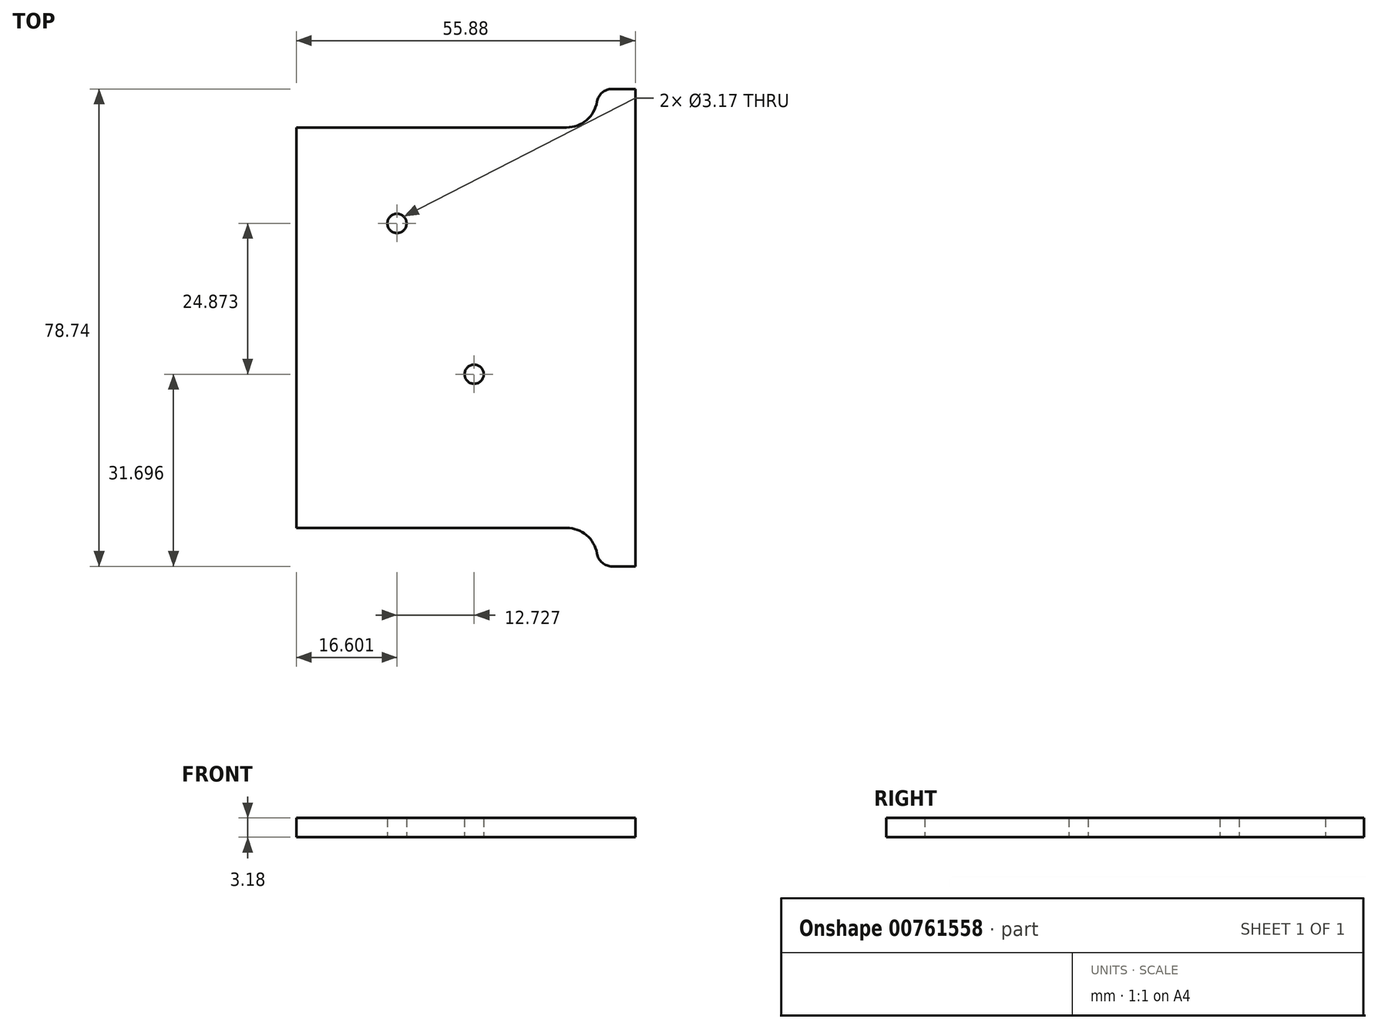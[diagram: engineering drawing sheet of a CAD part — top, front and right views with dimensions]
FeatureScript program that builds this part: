
annotation { "Feature Type Name" : "Feature", "Feature Type Description" : "" }
export const myFeature = defineFeature(function(context is Context, id is Id, definition is map)
    precondition{}
    {
        {
            var Q0;
            Q0=qCreatedBy(makeId("Top.planeOp"),FACE);
            var sketch = newSketch(context, id + "F0", { "sketchPlane" : qUnion([Q0])});
            skLineSegment(sketch, "E0.bottom", {"start": v(10.62, 7.25) * mm, "end": v(66.5, 7.25) * mm});
            skLineSegment(sketch, "E0.top", {"start": v(10.62, -58.79) * mm, "end": v(66.5, -58.79) * mm});
            skLineSegment(sketch, "E0.left", {"start": v(10.62, 7.25) * mm, "end": v(10.62, -58.79) * mm});
            skLineSegment(sketch, "E0.right", {"start": v(66.5, 7.25) * mm, "end": v(66.5, -58.79) * mm});
            skCircle(sketch, "E1", {"center": v(27.22, -8.57) * mm, "radius": 12.7 * mm});
            skCircle(sketch, "E2", {"center": v(27.22, -8.57) * mm, "radius": 6.35 * mm});
            skCircle(sketch, "E3", {"center": v(27.22, -8.57) * mm, "radius": 1.59 * mm});
            skCircle(sketch, "E4", {"center": v(39.95, -33.44) * mm, "radius": 21.59 * mm});
            skCircle(sketch, "E5", {"center": v(39.95, -33.44) * mm, "radius": 1.59 * mm});
            skLineSegment(sketch, "E6.bottom", {"start": v(66.5, -58.79) * mm, "end": v(60.15, -58.79) * mm});
            skLineSegment(sketch, "E6.top", {"start": v(66.5, -65.14) * mm, "end": v(60.15, -65.14) * mm});
            skLineSegment(sketch, "E6.left", {"start": v(66.5, -58.79) * mm, "end": v(66.5, -65.14) * mm});
            skLineSegment(sketch, "E6.right", {"start": v(60.15, -58.79) * mm, "end": v(60.15, -65.14) * mm});
            skLineSegment(sketch, "E7.bottom", {"start": v(66.5, 7.25) * mm, "end": v(60.15, 7.25) * mm});
            skLineSegment(sketch, "E7.top", {"start": v(66.5, 13.6) * mm, "end": v(60.15, 13.6) * mm});
            skLineSegment(sketch, "E7.left", {"start": v(66.5, 7.25) * mm, "end": v(66.5, 13.6) * mm});
            skLineSegment(sketch, "E7.right", {"start": v(60.15, 7.25) * mm, "end": v(60.15, 13.6) * mm});
            skSolve(sketch);
        }
        {
            var Q0;
            Q0 = qSketchRegion(id + "F0", true);
            extrude(context, id + "F1", {"entities" : qUnion([Q0]), "depth" : 3.17 * mm, "offsetDistance" : 25.4 * mm});
        }
        {
            var Q0;
            Q0=makeQuery(id+"F0.imprint","IMPRINT",FACE,{"disambiguationData":[TD([[makeQuery(id+"F0.imprint","IMPRINT",EDGE,{"derivedFrom":sQuery(id+"F0.wireOp",EDGE,"E0.bottom")}),-1.0]])]});
            var Q1;
            {var subQ4=sQuery(id+"F0.wireOp",EDGE,"E2");Q1=makeQuery(id+"F0.imprint","IMPRINT",FACE,{"disambiguationData":[TD([[makeQuery(id+"F0.imprint","IMPRINT",EDGE,{"derivedFrom":subQ4}),-1.0]])]});}
            var Q2;
            {var subQ0=sQuery(id+"F0.wireOp",EDGE,"E4");var subQ1=sQuery(id+"F0.wireOp",EDGE,"E1");var subQ2=makeQuery(id+"F0.imprint","INTERSECT",VERTEX,{"disambiguationData":[OD(0.0)],"derivedFrom":[subQ1,subQ0]});Q2=makeQuery(id+"F0.imprint","IMPRINT",FACE,{"disambiguationData":[TD([[makeQuery(id+"F0.imprint","IMPRINT",EDGE,{"disambiguationData":[TD([[subQ2,1.0]])],"derivedFrom":subQ1}),1.0]])]});}
            var Q3;
            Q3=makeQuery(id+"F0.imprint","IMPRINT",FACE,{"disambiguationData":[TD([[makeQuery(id+"F0.imprint","IMPRINT",EDGE,{"derivedFrom":sQuery(id+"F0.wireOp",EDGE,"E5")}),-1.0]])]});
            var Q4;
            Q4=makeQuery(id+"F0.imprint","IMPRINT",FACE,{"disambiguationData":[TD([[makeQuery(id+"F0.imprint","IMPRINT",EDGE,{"derivedFrom":sQuery(id+"F0.wireOp",EDGE,"E2")}),1.0]])]});
            extrude(context, id + "F2", {"entities" : qUnion([Q0, Q1, Q2, Q3, Q4]), "operationType" : NewBodyOperationType.ADD, "depth" : 3.17 * mm, "offsetDistance" : 25.4 * mm});
        }
        {
            var Q0;
            Q0=makeQuery(id+"F1.opExtrude","SWEPT_EDGE",EDGE,{"disambiguationData":[OSD([sQuery(id+"F0.wireOp",EDGE,"E6.top"),sQuery(id+"F0.wireOp",EDGE,"E6.right")])]});
            var Q1;
            Q1=makeQuery(id+"F1.opExtrude","SWEPT_EDGE",EDGE,{"disambiguationData":[OSD([sQuery(id+"F0.wireOp",EDGE,"E7.top"),sQuery(id+"F0.wireOp",EDGE,"E7.right")])]});
            fillet(context, id + "F3", {"entities" : qUnion([Q0, Q1]), "radius" : 2.54 * mm, "tangentPropagation" : true, "allowEdgeOverflow" : false});
        }
        {
            var Q0;
            Q0=makeQuery(id+"F1.opExtrude","SWEPT_EDGE",EDGE,{"disambiguationData":[OSD([sQuery(id+"F0.wireOp",EDGE,"E0.top"),sQuery(id+"F0.wireOp",EDGE,"E6.bottom"),sQuery(id+"F0.wireOp",EDGE,"E6.right")])]});
            var Q1;
            Q1=makeQuery(id+"F1.opExtrude","SWEPT_EDGE",EDGE,{"disambiguationData":[OSD([sQuery(id+"F0.wireOp",EDGE,"E0.bottom"),sQuery(id+"F0.wireOp",EDGE,"E7.bottom"),sQuery(id+"F0.wireOp",EDGE,"E7.right")])]});
            fillet(context, id + "F4", {"entities" : qUnion([Q0, Q1]), "radius" : 5.08 * mm, "tangentPropagation" : true, "allowEdgeOverflow" : false});
        }
    });
